# Revit family: Indoor_Pendant Lamp_Santa&Cole_Tekiò Circular
name_source: partatom
category: Luminarias
revit_build: Autodesk Revit 2018 (Build: 20190510_1515(x64)
units: mm (PartAtom-declared; Revit-internal decimal feet)

## family parameters
Anfitrión = Cara
Compartido = No
Corte con vacíos al cargar = No
Cota de conector redondo = Diámetro de uso
Origen de luz = Sí
Punto de cálculo de habitación = No
Tipo de pieza = Normal

## types (1)
- Indoor_Pendant Lamp_Santa&Cole_Tekiò Circular
    Archivo de red fotométrica = Tekio circular.IES
    Assembly Instructions - CE = https://www.santacole.com
    Assembly Instructions - UL = https://www.santacole.com
    Cambio de temperatura de color de luz atenuada = <Ninguno>
    Carga aparente = 200 W
    Code = TEKCE8+TEKCP8+TEKF02/TEKF03
    Elevación por defecto = 1219 mm
    Energy Label = https://www.santacole.com
    Fabricante = Santa & Cole
    Filtro de color = 16777215
    Lamp Shade Height = 102 mm
    Load = 200 W
    Manufacturer website = http://www.santacole.com
    Modelo = Tekiò Circular
    Screen Material = Santa&Cole - Washi Japanese Paper - Autoilluminated
    Structure Material = Santa&Cole - White Matte Finish
    Technical Information = https://www.santacole.com
    URL = https://www.santacole.com
    Voltaje (90-305 V) = 220 V
    Ángulo de inclinación = -90.00°

## geometry (parser evidence)
native form markers: Blend x4, Sweep x2
no freeform markers — native parametric forms only
